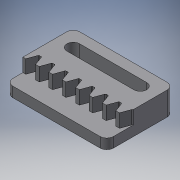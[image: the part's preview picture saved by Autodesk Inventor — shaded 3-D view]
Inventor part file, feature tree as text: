
AUTODESK INVENTOR PART (.ipt)
format: ipt  version: 2019 (Build 230136000, 136)  size: 196,608 bytes
history: native  units: in
note: dims shown in document units (in); Inventor stores cm internally (conversion verified against a paired STEP export)
features: extrude x2, sketch x2, pattern_linear x1, fillet x1
ambient origin geometry x8: Origin, YZ Plane, XZ Plane, XY Plane, X Axis, Y Axis, Z Axis, Center Point
bodies: Solid1 (feature_tree)
feature tree (6):
  extrude  "Extrusion1"  Depth=0.7874in
  extrude  "Extrusion4"  Depth=0.1969in
  pattern_linear  "Rectangular Pattern1"  Spacing1=0.1378in  [1 undecoded]
  fillet  "Fillet1"  Radius=0.01in
  sketch  "Sketch1"  dims[d0=1.1811in d1=0.7874in]
  sketch  "Sketch5"  dims[d6=0.2756in d7=0.0in d8=0.1969in d47=0.1378in d48=0.0in d49=0.01in d50=0.01in d51=0.0194in d52=0.0421in d53=0.112in d54=0.1189in d55=0.01in d57=3.937in d59=0.1571in d61=0.1495in d62=0.1495in d63=0.1969in d64=0.1969in d66=0.1969in d67=0.1969in d68=0.0787in]
note: 1 required parameter value undecoded (feature->parameter linkage not recoverable at this tier; creation-order binding heuristic only, values carry confidence <= 0.55)
